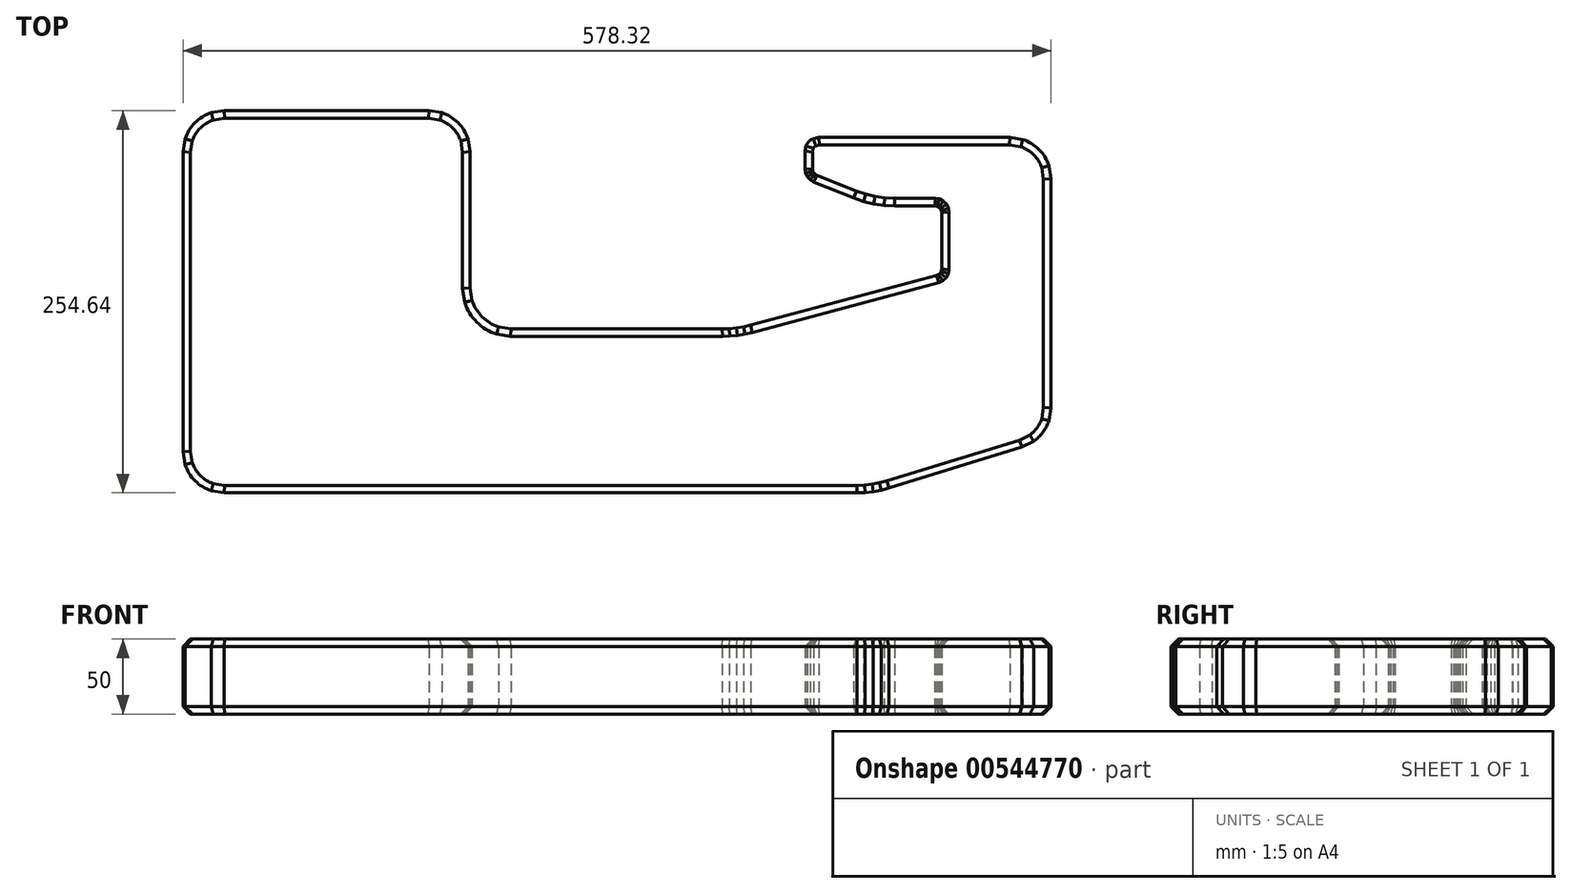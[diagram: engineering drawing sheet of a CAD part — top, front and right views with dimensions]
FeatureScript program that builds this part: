
annotation { "Feature Type Name" : "Feature", "Feature Type Description" : "" }
export const myFeature = defineFeature(function(context is Context, id is Id, definition is map)
    precondition{}
    {
        {
            var Q0;
            Q0=qCreatedBy(makeId("Top.planeOp"),FACE);
            var sketch = newSketch(context, id + "F0", { "sketchPlane" : qUnion([Q0])});
            skLineSegment(sketch, "E0", {"start": v(335.68, -23.32) * mm, "end": v(247.04, -50.59) * mm});
            skLineSegment(sketch, "E1", {"start": v(354.97, 155.66) * mm, "end": v(354.97, 2.8) * mm});
            skLineSegment(sketch, "E2", {"start": v(327.65, 182.98) * mm, "end": v(200.14, 182.98) * mm});
            skLineSegment(sketch, "E3", {"start": v(191.04, 173.88) * mm, "end": v(191.04, 161.83) * mm});
            skLineSegment(sketch, "E4", {"start": v(223.55, 142.66) * mm, "end": v(196.76, 153.37) * mm});
            skLineSegment(sketch, "E5", {"start": v(277.56, 137.45) * mm, "end": v(250.6, 137.45) * mm});
            skLineSegment(sketch, "E6", {"start": v(282.11, 132.9) * mm, "end": v(282.11, 95.4) * mm});
            skLineSegment(sketch, "E7", {"start": v(278.73, 91) * mm, "end": v(154.72, 57.94) * mm});
            skLineSegment(sketch, "E8", {"start": v(135.95, 55.48) * mm, "end": v(-4.77, 55.48) * mm});
            skLineSegment(sketch, "E9", {"start": v(-32.1, 173.51) * mm, "end": v(-32.1, 82.8) * mm});
            skLineSegment(sketch, "E10", {"start": v(-59.42, 200.83) * mm, "end": v(-196.03, 200.83) * mm});
            skLineSegment(sketch, "E11", {"start": v(-223.35, 173.51) * mm, "end": v(-223.35, -26.49) * mm});
            skLineSegment(sketch, "E12", {"start": v(-196.03, -53.81) * mm, "end": v(225.62, -53.81) * mm});
            skLineSegment(sketch, "E13", {"start": v(225.62, -53.81) * mm, "end": v(231.05, -53.6) * mm});
            skLineSegment(sketch, "E14", {"start": v(231.05, -53.6) * mm, "end": v(236.45, -53) * mm});
            skLineSegment(sketch, "E15", {"start": v(236.45, -53) * mm, "end": v(241.8, -52) * mm});
            skLineSegment(sketch, "E16", {"start": v(241.8, -52) * mm, "end": v(247.04, -50.59) * mm});
            skLineSegment(sketch, "E17", {"start": v(191.04, 161.83) * mm, "end": v(191.44, 159.16) * mm});
            skLineSegment(sketch, "E18", {"start": v(196.76, 153.37) * mm, "end": v(194.43, 154.73) * mm});
            skLineSegment(sketch, "E19", {"start": v(223.55, 142.66) * mm, "end": v(230.1, 140.4) * mm});
            skLineSegment(sketch, "E20", {"start": v(230.1, 140.4) * mm, "end": v(236.83, 138.76) * mm});
            skLineSegment(sketch, "E21", {"start": v(236.83, 138.76) * mm, "end": v(243.68, 137.78) * mm});
            skLineSegment(sketch, "E22", {"start": v(243.68, 137.78) * mm, "end": v(250.6, 137.45) * mm});
            skLineSegment(sketch, "E23", {"start": v(277.56, 137.45) * mm, "end": v(278.96, 137.22) * mm});
            skLineSegment(sketch, "E24", {"start": v(278.96, 137.22) * mm, "end": v(280.23, 136.58) * mm});
            skLineSegment(sketch, "E25", {"start": v(282.11, 95.4) * mm, "end": v(281.87, 93.94) * mm});
            skLineSegment(sketch, "E26", {"start": v(281.87, 93.94) * mm, "end": v(281.17, 92.63) * mm});
            skLineSegment(sketch, "E27", {"start": v(281.17, 92.63) * mm, "end": v(280.08, 91.62) * mm});
            skLineSegment(sketch, "E28", {"start": v(280.08, 91.62) * mm, "end": v(278.73, 91) * mm});
            skLineSegment(sketch, "E29", {"start": v(154.72, 57.94) * mm, "end": v(150.1, 56.87) * mm});
            skLineSegment(sketch, "E30", {"start": v(150.1, 56.87) * mm, "end": v(145.42, 56.1) * mm});
            skLineSegment(sketch, "E31", {"start": v(145.42, 56.1) * mm, "end": v(140.7, 55.63) * mm});
            skLineSegment(sketch, "E32", {"start": v(140.7, 55.63) * mm, "end": v(135.95, 55.48) * mm});
            skLineSegment(sketch, "E33", {"start": v(282.11, 132.9) * mm, "end": v(281.89, 134.3) * mm});
            skLineSegment(sketch, "E34", {"start": v(281.89, 134.3) * mm, "end": v(281.24, 135.57) * mm});
            skLineSegment(sketch, "E35", {"start": v(281.24, 135.57) * mm, "end": v(280.23, 136.58) * mm});
            skLineSegment(sketch, "E36", {"start": v(194.43, 154.73) * mm, "end": v(192.6, 156.72) * mm});
            skLineSegment(sketch, "E37", {"start": v(192.6, 156.72) * mm, "end": v(191.44, 159.16) * mm});
            skLineSegment(sketch, "E38", {"start": v(-223.35, -26.49) * mm, "end": v(-222.02, -34.93) * mm});
            skArc(sketch, "E39", {"start": v(-222.02, -34.93) * mm, "mid": v(-215.35, -45.8) * mm, "end": v(-204.47, -52.47) * mm});
            skLineSegment(sketch, "E40", {"start": v(-204.47, -52.47) * mm, "end": v(-196.03, -53.81) * mm});
            skLineSegment(sketch, "E41", {"start": v(-196.03, 200.83) * mm, "end": v(-204.47, 199.5) * mm});
            skArc(sketch, "E42", {"start": v(-204.47, 199.5) * mm, "mid": v(-215.35, 192.83) * mm, "end": v(-222.02, 181.95) * mm});
            skLineSegment(sketch, "E43", {"start": v(-222.02, 181.95) * mm, "end": v(-223.35, 173.51) * mm});
            skLineSegment(sketch, "E44", {"start": v(-32.1, 173.51) * mm, "end": v(-33.43, 181.95) * mm});
            skArc(sketch, "E45", {"start": v(-33.43, 181.95) * mm, "mid": v(-40.1, 192.83) * mm, "end": v(-50.98, 199.5) * mm});
            skLineSegment(sketch, "E46", {"start": v(-50.98, 199.5) * mm, "end": v(-59.42, 200.83) * mm});
            skLineSegment(sketch, "E47", {"start": v(-4.77, 55.48) * mm, "end": v(-13.22, 56.82) * mm});
            skArc(sketch, "E48", {"start": v(-30.76, 74.36) * mm, "mid": v(-24.1, 63.48) * mm, "end": v(-13.22, 56.82) * mm});
            skLineSegment(sketch, "E49", {"start": v(-30.76, 74.36) * mm, "end": v(-32.1, 82.8) * mm});
            skLineSegment(sketch, "E50", {"start": v(200.14, 182.98) * mm, "end": v(196.66, 182.29) * mm});
            skArc(sketch, "E51", {"start": v(196.66, 182.29) * mm, "mid": v(193.7, 180.32) * mm, "end": v(191.73, 177.36) * mm});
            skLineSegment(sketch, "E52", {"start": v(191.73, 177.36) * mm, "end": v(191.04, 173.88) * mm});
            skLineSegment(sketch, "E53", {"start": v(354.97, 155.66) * mm, "end": v(353.63, 164.1) * mm});
            skArc(sketch, "E54", {"start": v(353.63, 164.1) * mm, "mid": v(346.97, 174.98) * mm, "end": v(336.1, 181.65) * mm});
            skLineSegment(sketch, "E55", {"start": v(336.1, 181.65) * mm, "end": v(327.65, 182.98) * mm});
            skLineSegment(sketch, "E56", {"start": v(335.68, -23.32) * mm, "end": v(343.45, -19.5) * mm});
            skArc(sketch, "E57", {"start": v(343.45, -19.5) * mm, "mid": v(349.63, -13.43) * mm, "end": v(353.6, -5.75) * mm});
            skLineSegment(sketch, "E58", {"start": v(353.6, -5.75) * mm, "end": v(354.97, 2.8) * mm});
            skLineSegment(sketch, "E59", {"start": v(354.97, 2.8) * mm, "end": v(353.6, -5.75) * mm});
            skLineSegment(sketch, "E60", {"start": v(343.45, -19.5) * mm, "end": v(335.68, -23.32) * mm});
            skLineSegment(sketch, "E61", {"start": v(327.65, 182.98) * mm, "end": v(336.1, 181.65) * mm});
            skLineSegment(sketch, "E62", {"start": v(353.63, 164.1) * mm, "end": v(354.97, 155.66) * mm});
            skLineSegment(sketch, "E63", {"start": v(191.04, 173.88) * mm, "end": v(191.73, 177.36) * mm});
            skLineSegment(sketch, "E64", {"start": v(196.66, 182.29) * mm, "end": v(200.14, 182.98) * mm});
            skLineSegment(sketch, "E65", {"start": v(-32.1, 82.8) * mm, "end": v(-30.76, 74.36) * mm});
            skLineSegment(sketch, "E66", {"start": v(-13.22, 56.82) * mm, "end": v(-4.77, 55.48) * mm});
            skLineSegment(sketch, "E67", {"start": v(-59.42, 200.83) * mm, "end": v(-50.98, 199.5) * mm});
            skLineSegment(sketch, "E68", {"start": v(-33.43, 181.95) * mm, "end": v(-32.1, 173.51) * mm});
            skLineSegment(sketch, "E69", {"start": v(-223.35, 173.51) * mm, "end": v(-222.02, 181.95) * mm});
            skLineSegment(sketch, "E70", {"start": v(-204.47, 199.5) * mm, "end": v(-196.03, 200.83) * mm});
            skLineSegment(sketch, "E71", {"start": v(-196.03, -53.81) * mm, "end": v(-204.47, -52.47) * mm});
            skLineSegment(sketch, "E72", {"start": v(-222.02, -34.93) * mm, "end": v(-223.35, -26.49) * mm});
            skSolve(sketch);
        }
        {
            var Q0;
            Q0=makeQuery(id+"F0.imprint","IMPRINT",FACE,{"disambiguationData":[TD([[makeQuery(id+"F0.imprint","IMPRINT",EDGE,{"derivedFrom":sQuery(id+"F0.wireOp",EDGE,"E0")}),-1.0]])]});
            extrude(context, id + "F1", {"entities" : qUnion([Q0]), "depth" : 50 * mm, "offsetDistance" : 25 * mm});
        }
        {
            var Q0;
            Q0=makeQuery(id+"F1.opExtrude","CAP_FACE",FACE,{"disambiguationData":[OSD([sQuery(id+"F0.wireOp",EDGE,"E0"),sQuery(id+"F0.wireOp",EDGE,"E1"),sQuery(id+"F0.wireOp",EDGE,"E2"),sQuery(id+"F0.wireOp",EDGE,"E3"),sQuery(id+"F0.wireOp",EDGE,"E4"),sQuery(id+"F0.wireOp",EDGE,"E5"),sQuery(id+"F0.wireOp",EDGE,"E6"),sQuery(id+"F0.wireOp",EDGE,"E7"),sQuery(id+"F0.wireOp",EDGE,"E8"),sQuery(id+"F0.wireOp",EDGE,"E9"),sQuery(id+"F0.wireOp",EDGE,"E10"),sQuery(id+"F0.wireOp",EDGE,"E11"),sQuery(id+"F0.wireOp",EDGE,"E12"),sQuery(id+"F0.wireOp",EDGE,"E13"),sQuery(id+"F0.wireOp",EDGE,"E14"),sQuery(id+"F0.wireOp",EDGE,"E15"),sQuery(id+"F0.wireOp",EDGE,"E16"),sQuery(id+"F0.wireOp",EDGE,"E17"),sQuery(id+"F0.wireOp",EDGE,"E18"),sQuery(id+"F0.wireOp",EDGE,"E19"),sQuery(id+"F0.wireOp",EDGE,"E20"),sQuery(id+"F0.wireOp",EDGE,"E21"),sQuery(id+"F0.wireOp",EDGE,"E22"),sQuery(id+"F0.wireOp",EDGE,"E23"),sQuery(id+"F0.wireOp",EDGE,"E24"),sQuery(id+"F0.wireOp",EDGE,"E25"),sQuery(id+"F0.wireOp",EDGE,"E26"),sQuery(id+"F0.wireOp",EDGE,"E27"),sQuery(id+"F0.wireOp",EDGE,"E28"),sQuery(id+"F0.wireOp",EDGE,"E29"),sQuery(id+"F0.wireOp",EDGE,"E30"),sQuery(id+"F0.wireOp",EDGE,"E31"),sQuery(id+"F0.wireOp",EDGE,"E32"),sQuery(id+"F0.wireOp",EDGE,"E33"),sQuery(id+"F0.wireOp",EDGE,"E34"),sQuery(id+"F0.wireOp",EDGE,"E35"),sQuery(id+"F0.wireOp",EDGE,"E36"),sQuery(id+"F0.wireOp",EDGE,"E37"),sQuery(id+"F0.wireOp",EDGE,"E59"),sQuery(id+"F0.wireOp",EDGE,"E57"),sQuery(id+"F0.wireOp",EDGE,"E60"),sQuery(id+"F0.wireOp",EDGE,"E61"),sQuery(id+"F0.wireOp",EDGE,"E54"),sQuery(id+"F0.wireOp",EDGE,"E62"),sQuery(id+"F0.wireOp",EDGE,"E63"),sQuery(id+"F0.wireOp",EDGE,"E51"),sQuery(id+"F0.wireOp",EDGE,"E64"),sQuery(id+"F0.wireOp",EDGE,"E65"),sQuery(id+"F0.wireOp",EDGE,"E48"),sQuery(id+"F0.wireOp",EDGE,"E66"),sQuery(id+"F0.wireOp",EDGE,"E67"),sQuery(id+"F0.wireOp",EDGE,"E45"),sQuery(id+"F0.wireOp",EDGE,"E68"),sQuery(id+"F0.wireOp",EDGE,"E69"),sQuery(id+"F0.wireOp",EDGE,"E42"),sQuery(id+"F0.wireOp",EDGE,"E70"),sQuery(id+"F0.wireOp",EDGE,"E71"),sQuery(id+"F0.wireOp",EDGE,"E39"),sQuery(id+"F0.wireOp",EDGE,"E72")])],"isStart":true});
            var Q1;
            Q1=makeQuery(id+"F1.opExtrude","CAP_FACE",FACE,{"disambiguationData":[OSD([sQuery(id+"F0.wireOp",EDGE,"E0"),sQuery(id+"F0.wireOp",EDGE,"E1"),sQuery(id+"F0.wireOp",EDGE,"E2"),sQuery(id+"F0.wireOp",EDGE,"E3"),sQuery(id+"F0.wireOp",EDGE,"E4"),sQuery(id+"F0.wireOp",EDGE,"E5"),sQuery(id+"F0.wireOp",EDGE,"E6"),sQuery(id+"F0.wireOp",EDGE,"E7"),sQuery(id+"F0.wireOp",EDGE,"E8"),sQuery(id+"F0.wireOp",EDGE,"E9"),sQuery(id+"F0.wireOp",EDGE,"E10"),sQuery(id+"F0.wireOp",EDGE,"E11"),sQuery(id+"F0.wireOp",EDGE,"E12"),sQuery(id+"F0.wireOp",EDGE,"E13"),sQuery(id+"F0.wireOp",EDGE,"E14"),sQuery(id+"F0.wireOp",EDGE,"E15"),sQuery(id+"F0.wireOp",EDGE,"E16"),sQuery(id+"F0.wireOp",EDGE,"E17"),sQuery(id+"F0.wireOp",EDGE,"E18"),sQuery(id+"F0.wireOp",EDGE,"E19"),sQuery(id+"F0.wireOp",EDGE,"E20"),sQuery(id+"F0.wireOp",EDGE,"E21"),sQuery(id+"F0.wireOp",EDGE,"E22"),sQuery(id+"F0.wireOp",EDGE,"E23"),sQuery(id+"F0.wireOp",EDGE,"E24"),sQuery(id+"F0.wireOp",EDGE,"E25"),sQuery(id+"F0.wireOp",EDGE,"E26"),sQuery(id+"F0.wireOp",EDGE,"E27"),sQuery(id+"F0.wireOp",EDGE,"E28"),sQuery(id+"F0.wireOp",EDGE,"E29"),sQuery(id+"F0.wireOp",EDGE,"E30"),sQuery(id+"F0.wireOp",EDGE,"E31"),sQuery(id+"F0.wireOp",EDGE,"E32"),sQuery(id+"F0.wireOp",EDGE,"E33"),sQuery(id+"F0.wireOp",EDGE,"E34"),sQuery(id+"F0.wireOp",EDGE,"E35"),sQuery(id+"F0.wireOp",EDGE,"E36"),sQuery(id+"F0.wireOp",EDGE,"E37"),sQuery(id+"F0.wireOp",EDGE,"E59"),sQuery(id+"F0.wireOp",EDGE,"E57"),sQuery(id+"F0.wireOp",EDGE,"E60"),sQuery(id+"F0.wireOp",EDGE,"E61"),sQuery(id+"F0.wireOp",EDGE,"E54"),sQuery(id+"F0.wireOp",EDGE,"E62"),sQuery(id+"F0.wireOp",EDGE,"E63"),sQuery(id+"F0.wireOp",EDGE,"E51"),sQuery(id+"F0.wireOp",EDGE,"E64"),sQuery(id+"F0.wireOp",EDGE,"E65"),sQuery(id+"F0.wireOp",EDGE,"E48"),sQuery(id+"F0.wireOp",EDGE,"E66"),sQuery(id+"F0.wireOp",EDGE,"E67"),sQuery(id+"F0.wireOp",EDGE,"E45"),sQuery(id+"F0.wireOp",EDGE,"E68"),sQuery(id+"F0.wireOp",EDGE,"E69"),sQuery(id+"F0.wireOp",EDGE,"E42"),sQuery(id+"F0.wireOp",EDGE,"E70"),sQuery(id+"F0.wireOp",EDGE,"E71"),sQuery(id+"F0.wireOp",EDGE,"E39"),sQuery(id+"F0.wireOp",EDGE,"E72")])],"isStart":false});
            chamfer(context, id + "F2", {"entities" : qUnion([Q0, Q1]), "width" : 5 * mm, "tangentPropagation" : true});
        }
    });
